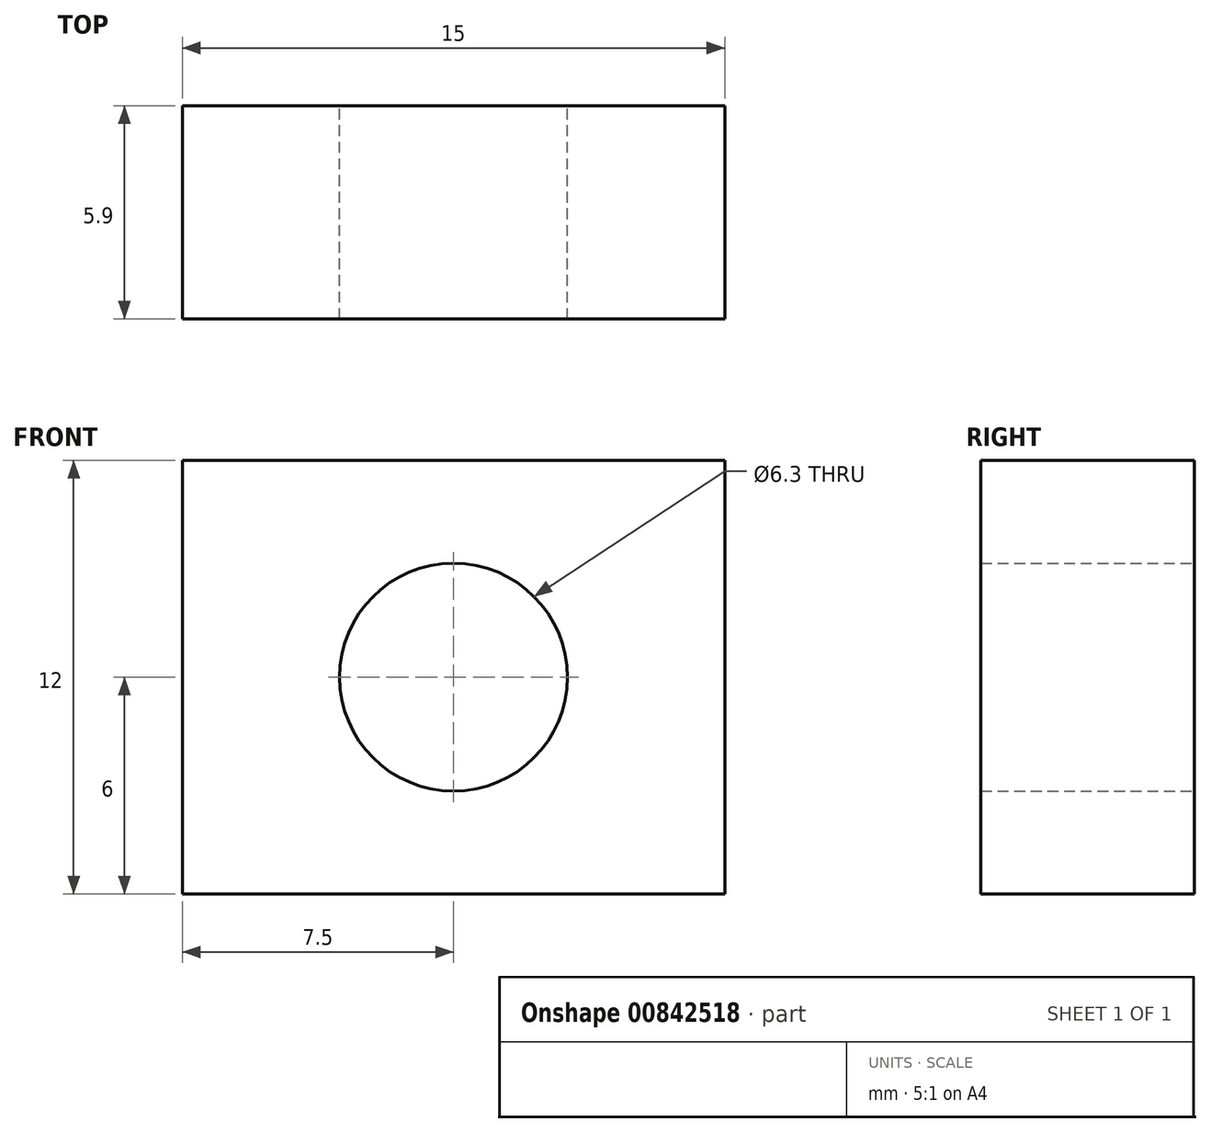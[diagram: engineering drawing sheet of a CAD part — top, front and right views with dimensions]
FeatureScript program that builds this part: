
annotation { "Feature Type Name" : "Feature", "Feature Type Description" : "" }
export const myFeature = defineFeature(function(context is Context, id is Id, definition is map)
    precondition{}
    {
        {
            var Q0;
            Q0=qCreatedBy(makeId("Front.planeOp"),FACE);
            var sketch = newSketch(context, id + "F0", { "sketchPlane" : qUnion([Q0])});
            skLineSegment(sketch, "E0.bottom", {"start": v(-7.5, 6) * mm, "end": v(7.5, 6) * mm});
            skLineSegment(sketch, "E0.top", {"start": v(-7.5, -6) * mm, "end": v(7.5, -6) * mm});
            skLineSegment(sketch, "E0.left", {"start": v(-7.5, 6) * mm, "end": v(-7.5, -6) * mm});
            skLineSegment(sketch, "E0.right", {"start": v(7.5, 6) * mm, "end": v(7.5, -6) * mm});
            skCircle(sketch, "E1", {"center": v(0, 0) * mm, "radius": 3.15 * mm});
            skSolve(sketch);
        }
        {
            var Q0;
            Q0=makeQuery(id+"F0.imprint","IMPRINT",FACE,{"disambiguationData":[TD([[makeQuery(id+"F0.imprint","IMPRINT",EDGE,{"derivedFrom":sQuery(id+"F0.wireOp",EDGE,"E0.bottom")}),-1.0]])]});
            extrude(context, id + "F1", {"entities" : qUnion([Q0]), "depth" : 5.9 * mm, "offsetDistance" : 25 * mm});
        }
    });
